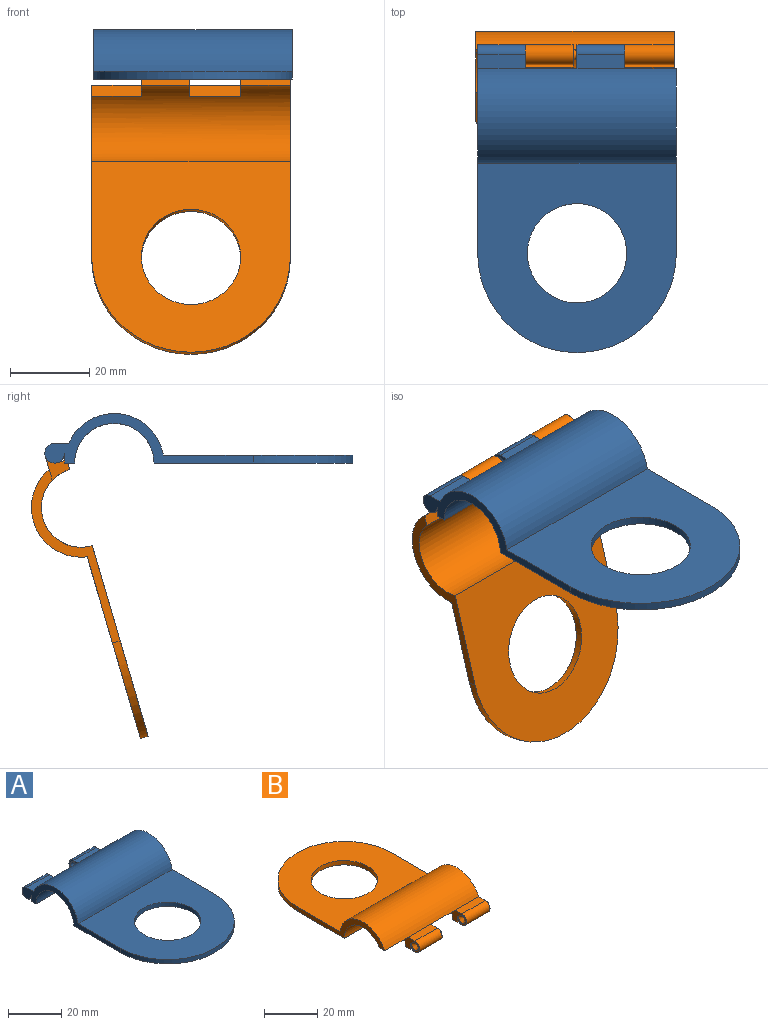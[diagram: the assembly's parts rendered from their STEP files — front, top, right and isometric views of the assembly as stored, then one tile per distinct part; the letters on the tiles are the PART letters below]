
ASSEMBLY  parts=2 mates=1
PART A: 24 faces, bbox 50x77.5x12.5 mm
  f0: plane 12x2.5mm, normal (0,0,-1), area 30mm2, adj f2,f17,f18,f19
  f1: plane 12x2.5mm, normal (0,0,-1), area 30mm2, adj f2,f4,f12,f13
  f2: cylinder r=10mm len=50mm, axis (1,0,0), area 1434.7mm2, adj f0,f1,f4,f6,f9,f13,f18,f19
  f3: cylinder r=12.5mm len=50mm, axis (1,0,0), area 1605.9mm2, adj f4,f6,f8,f10,f16,f22,f23
  f4: plane 52.5x12.5mm, normal (-1,0,0), area 156.1mm2, adj f1,f2,f3,f5,f8,f9,f10,f11
  f5: cylinder r=25mm len=50mm, axis (0,0,-1), area 157.1mm2, adj f4,f6,f8,f9
  f6: plane 46.46x12.5mm, normal (1,0,0), area 120.5mm2, adj f2,f3,f5,f8,f9,f23
  f7: cylinder r=12.5mm len=25mm, axis (0,0,-1), area 157.1mm2, adj f8,f9
  f8: plane 50x47.66mm, normal (0,0,1), area 1623.9mm2, adj f3,f4,f5,f6,f7
  f9: plane 50x50mm, normal (0,0,-1), area 1740.9mm2, adj f2,f4,f5,f6,f7
  f10: plane 12x3.54mm, normal (0,0,1), area 42.5mm2, adj f3,f4,f11,f13
  f11: cylinder r=2.5mm len=12mm, axis (-1,0,0), area 141.4mm2, adj f4,f10,f12,f13
  f12: plane 12x2.5mm, normal (0,1,0), area 30mm2, adj f1,f4,f11,f13
  f13: plane 8.84x5mm, normal (1,0,0), area 28.6mm2, adj f1,f2,f10,f11,f12,f14,f22
  f14: cone r=0mm half-angle=36.9deg, axis (-1,0,0), area 11.8mm2, adj f13
  f15: cylinder r=2.5mm len=12mm, axis (-1,0,0), area 141.4mm2, adj f16,f17,f18,f19
  f16: plane 12x3.54mm, normal (0,0,1), area 42.5mm2, adj f3,f15,f18,f19
  f17: plane 12x2.5mm, normal (0,1,0), area 30mm2, adj f0,f15,f18,f19
  f18: plane 8.84x5mm, normal (1,0,0), area 28.6mm2, adj f0,f2,f15,f16,f17,f20,f23
  f19: plane 8.84x5mm, normal (-1,0,0), area 26mm2, adj f0,f2,f15,f16,f17,f21,f22
  f20: cone r=0mm half-angle=36.9deg, axis (-1,0,0), area 11.8mm2, adj f18
  f21: cone r=0mm half-angle=35deg, axis (-1,0,0), area 16.8mm2, adj f19
  f22: plane 13x2.8mm, normal (0,0,-1), area 36.4mm2, adj f2,f3,f13,f19
  f23: plane 13x2.8mm, normal (0,0,-1), area 36.4mm2, adj f2,f3,f6,f18
PART B: 24 faces, bbox 50x77.5x12.5 mm
  f0: plane 12.5x2.5mm, normal (0,0,-1), area 31.3mm2, adj f10,f11,f17,f18
  f1: plane 50x50mm, normal (0,0,-1), area 1740.9mm2, adj f10,f11,f13,f20,f21
  f2: cylinder r=2.5mm len=12mm, axis (-1,0,0), area 141.4mm2, adj f3,f4,f5,f6
  f3: plane 12x2.5mm, normal (0,-1,0), area 30mm2, adj f2,f5,f6,f12
  f4: plane 12x3.54mm, normal (0,0,1), area 42.5mm2, adj f2,f5,f6,f9
  f5: plane 8.84x5mm, normal (1,0,0), area 28.6mm2, adj f2,f3,f4,f8,f11,f12,f23
  f6: plane 8.84x5mm, normal (-1,0,0), area 26mm2, adj f2,f3,f4,f7,f11,f12,f22
  f7: cone r=0mm half-angle=35deg, axis (-1,0,0), area 16.8mm2, adj f6
  f8: cone r=0mm half-angle=36.9deg, axis (-1,0,0), area 11.8mm2, adj f5
  f9: cylinder r=12.5mm len=50mm, axis (-1,0,0), area 1605.9mm2, adj f4,f10,f13,f14,f15,f22,f23
  f10: plane 52.5x12.5mm, normal (1,0,0), area 156.1mm2, adj f0,f1,f9,f11,f14,f15,f16,f17
  f11: cylinder r=10mm len=50mm, axis (-1,0,0), area 1437.3mm2, adj f0,f1,f5,f6,f10,f12,f13,f18
  f12: plane 12x2.5mm, normal (0,0,-1), area 30mm2, adj f3,f5,f6,f11
  f13: plane 46.46x12.5mm, normal (-1,0,0), area 120.5mm2, adj f1,f9,f11,f14,f20,f22
  f14: plane 50x47.66mm, normal (0,0,1), area 1623.9mm2, adj f9,f10,f13,f20,f21
  f15: plane 12.5x3.54mm, normal (0,0,1), area 44.3mm2, adj f9,f10,f16,f18
  f16: cylinder r=2.5mm len=12.5mm, axis (1,0,0), area 147.3mm2, adj f10,f15,f17,f18
  f17: plane 12.5x2.5mm, normal (0,-1,0), area 31.2mm2, adj f0,f10,f16,f18
  f18: plane 8.84x5mm, normal (-1,0,0), area 26mm2, adj f0,f11,f15,f16,f17,f19,f23
  f19: cone r=0mm half-angle=35deg, axis (-1,0,0), area 16.8mm2, adj f18
  f20: cylinder r=25mm len=50mm, axis (0,0,1), area 157.1mm2, adj f1,f10,f13,f14
  f21: cylinder r=12.5mm len=25mm, axis (0,0,1), area 157.1mm2, adj f1,f14
  f22: plane 12.5x2.8mm, normal (0,0,-1), area 35mm2, adj f6,f9,f11,f13
  f23: plane 13x2.8mm, normal (0,0,-1), area 36.4mm2, adj f5,f9,f11,f18
PLACE A t=(-10.7,-12.03,11.1)mm fixed
PLACE B rot(axis=(-1,0,0),106.3deg) t=(-11.2,49.65,62.28)mm
MATE revolute B.f7 <-> A.f11  axis (-1,0,0) through (1.3,37.97,13.6)mm
